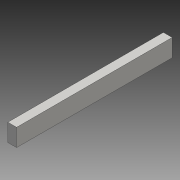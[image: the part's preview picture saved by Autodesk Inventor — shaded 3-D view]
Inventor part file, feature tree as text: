
AUTODESK INVENTOR PART (.ipt)
format: ipt  version: 2016 (Build 200138000, 138)  size: 69,120 bytes
history: native  units: mm
features: extrude x1, sketch x1
ambient origin geometry x8: Origin, YZ Plane, XZ Plane, XY Plane, X Axis, Y Axis, Z Axis, Center Point
bodies: 实体1 (feature_tree)
feature tree (2):
  extrude  "拉伸1"  Depth=20.0mm
  sketch  "草图1"  dims[d0=40.0mm d1=20.0mm d2=354.299mm d3=0.0mm]
